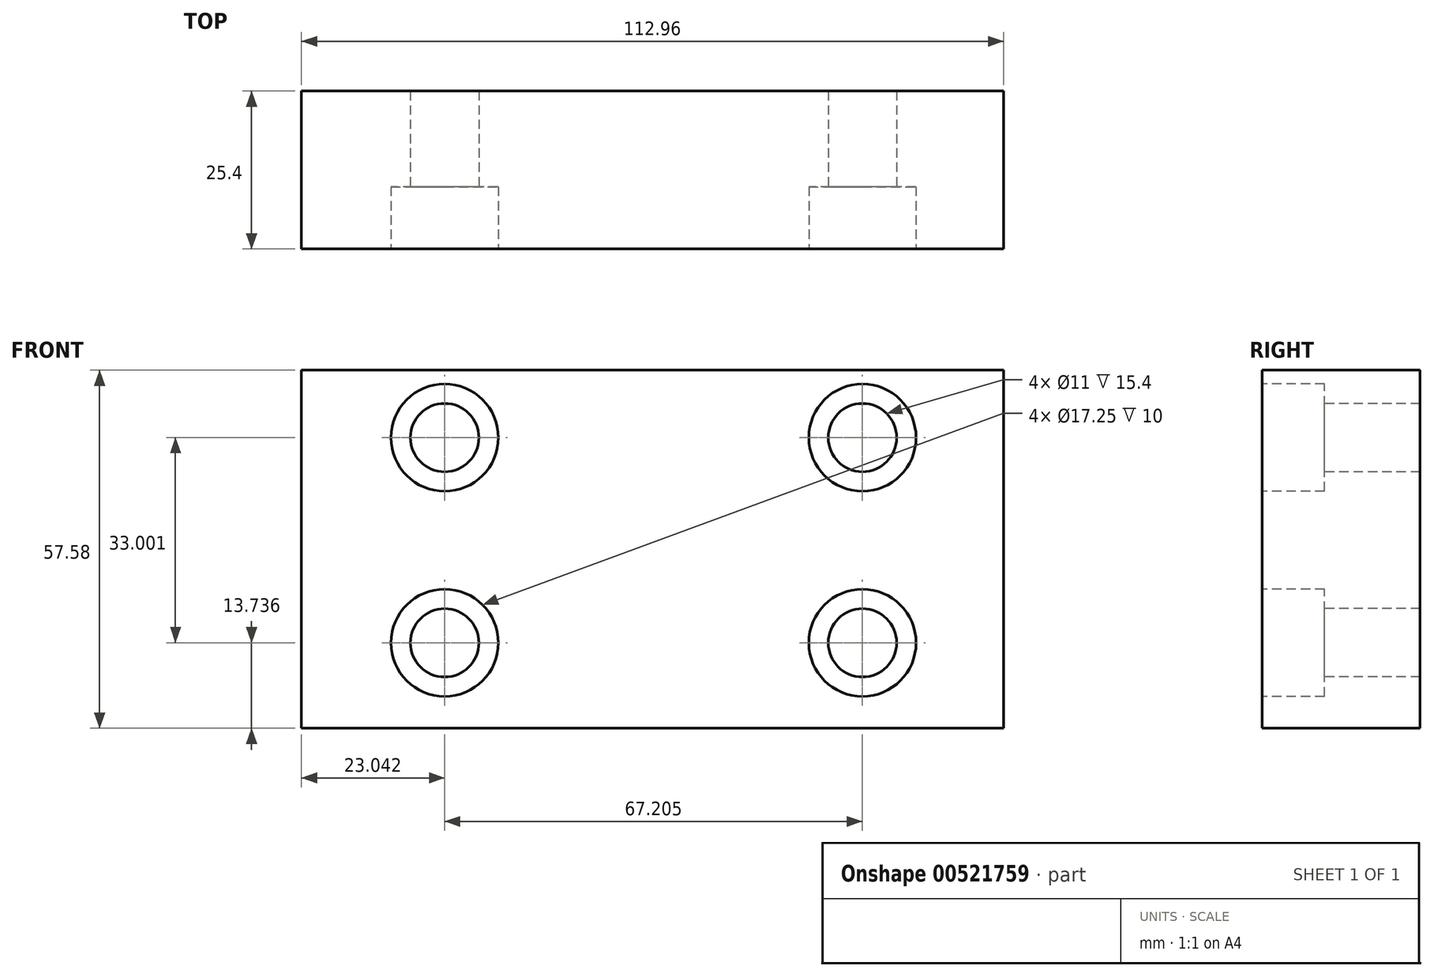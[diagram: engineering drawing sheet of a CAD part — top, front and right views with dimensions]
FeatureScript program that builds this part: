
annotation { "Feature Type Name" : "Feature", "Feature Type Description" : "" }
export const myFeature = defineFeature(function(context is Context, id is Id, definition is map)
    precondition{}
    {
        {
            var Q0;
            Q0=qCreatedBy(makeId("Front.planeOp"),FACE);
            var sketch = newSketch(context, id + "F0", { "sketchPlane" : qUnion([Q0])});
            skLineSegment(sketch, "E0.bottom", {"start": v(-48.16, 22.24) * mm, "end": v(64.8, 22.24) * mm});
            skLineSegment(sketch, "E0.top", {"start": v(-48.16, -35.34) * mm, "end": v(64.8, -35.34) * mm});
            skLineSegment(sketch, "E0.left", {"start": v(-48.16, 22.24) * mm, "end": v(-48.16, -35.34) * mm});
            skLineSegment(sketch, "E0.right", {"start": v(64.8, 22.24) * mm, "end": v(64.8, -35.34) * mm});
            skSolve(sketch);
        }
        {
            var Q0;
            Q0 = qSketchRegion(id + "F0", true);
            extrude(context, id + "F1", {"entities" : qUnion([Q0]), "depth" : 25.4 * mm, "offsetDistance" : 25.4 * mm});
        }
        {
            var Q0;
            Q0=makeQuery(id+"F1.opExtrude","CAP_FACE",FACE,{"disambiguationData":[OSD([sQuery(id+"F0.wireOp",EDGE,"E0.bottom"),sQuery(id+"F0.wireOp",EDGE,"E0.top"),sQuery(id+"F0.wireOp",EDGE,"E0.left"),sQuery(id+"F0.wireOp",EDGE,"E0.right")])],"isStart":false});
            var sketch = newSketch(context, id + "F2", { "sketchPlane" : qUnion([Q0])});
            skLineSegment(sketch, "E1.bottom", {"start": v(-25.12, 11.4) * mm, "end": v(42.09, 11.4) * mm, "construction": true});
            skLineSegment(sketch, "E1.top", {"start": v(-25.12, -21.6) * mm, "end": v(42.09, -21.6) * mm, "construction": true});
            skLineSegment(sketch, "E1.left", {"start": v(-25.12, 11.4) * mm, "end": v(-25.12, -21.6) * mm, "construction": true});
            skLineSegment(sketch, "E1.right", {"start": v(42.09, 11.4) * mm, "end": v(42.09, -21.6) * mm, "construction": true});
            skPoint(sketch, "E2", {"position": v(-25.12, 11.4) * mm});
            skPoint(sketch, "E3", {"position": v(42.09, 11.4) * mm});
            skPoint(sketch, "E4", {"position": v(42.09, -21.6) * mm});
            skPoint(sketch, "E5", {"position": v(-25.12, -21.6) * mm});
            skSolve(sketch);
        }
        {
            var Q0;
            Q0=sQuery(id+"F2.wireOp",VERTEX,"E2");
            var Q1;
            Q1=sQuery(id+"F2.wireOp",VERTEX,"E5");
            var Q2;
            Q2=sQuery(id+"F2.wireOp",VERTEX,"E3");
            var Q3;
            Q3=sQuery(id+"F2.wireOp",VERTEX,"E4");
            var Q4;
            Q4=makeQuery(id+"F1.opExtrude","SWEPT_BODY",BODY,{"disambiguationData":[OSD([sQuery(id+"F0.wireOp",EDGE,"E0.bottom"),sQuery(id+"F0.wireOp",EDGE,"E0.top"),sQuery(id+"F0.wireOp",EDGE,"E0.left"),sQuery(id+"F0.wireOp",EDGE,"E0.right")])]});
            hole(context, id + "F3", {"style" : HoleStyle.C_BORE, "endStyle" : HoleEndStyle.THROUGH, "standardTappedOrClearance" : lookupTablePath({ "standard" : "ISO", "fit" : "Normal", "size" : "M10", "type" : "Clearance" }), "standardBlindInLast" : lookupTablePath({ "fit" : "Standard", "standard" : "ISO", "size" : "M10", "type" : "Clearance" }), "holeDiameter" : 11 * mm, "cBoreDiameter" : 17.25 * mm, "cBoreDepth" : 10 * mm, "isTappedThrough" : true, "tappedDepth" : 12.7 * mm, "tapClearance" : 3, "locations" : qUnion([Q0, Q1, Q2, Q3]), "scope" : qUnion([Q4])});
        }
    });
